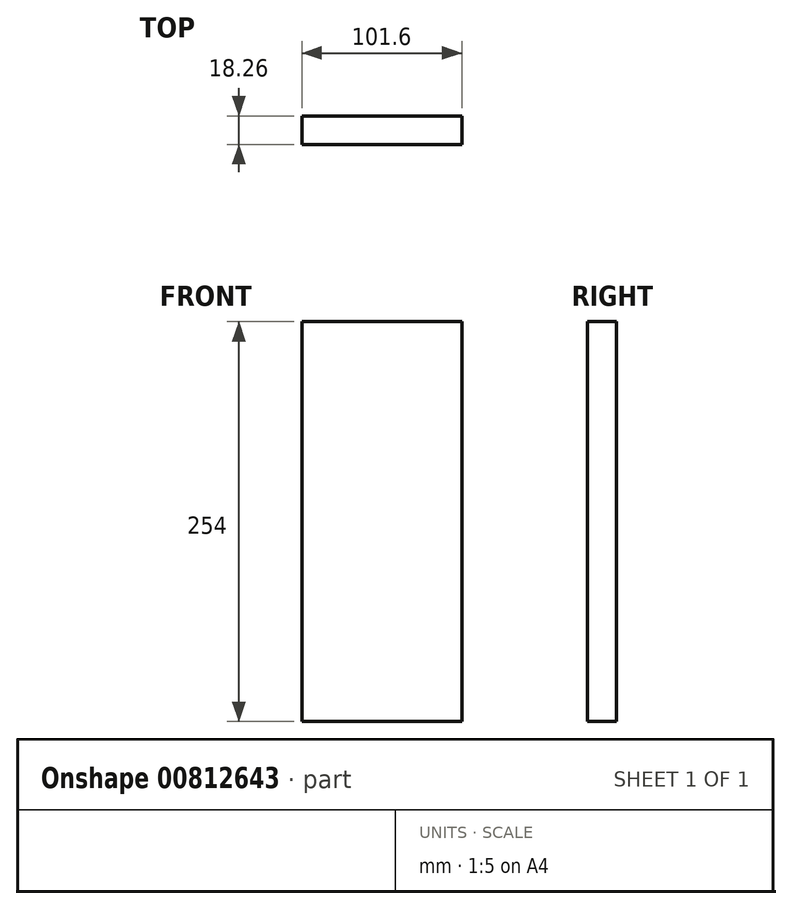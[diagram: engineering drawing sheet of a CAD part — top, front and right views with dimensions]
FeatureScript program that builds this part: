
annotation { "Feature Type Name" : "Feature", "Feature Type Description" : "" }
export const myFeature = defineFeature(function(context is Context, id is Id, definition is map)
    precondition{}
    {
        {
            var Q0;
            Q0=qCreatedBy(makeId("Front.planeOp"),FACE);
            var sketch = newSketch(context, id + "F0", { "sketchPlane" : qUnion([Q0])});
            skLineSegment(sketch, "E0.bottom", {"start": v(50.8, 127) * mm, "end": v(-50.8, 127) * mm});
            skLineSegment(sketch, "E0.top", {"start": v(50.8, -127) * mm, "end": v(-50.8, -127) * mm});
            skLineSegment(sketch, "E0.left", {"start": v(50.8, 127) * mm, "end": v(50.8, -127) * mm});
            skLineSegment(sketch, "E0.right", {"start": v(-50.8, 127) * mm, "end": v(-50.8, -127) * mm});
            skPoint(sketch, "E0.middle", {"position": v(0, 0) * mm});
            skSolve(sketch);
        }
        {
            var Q0;
            Q0=qSketchRegion(id+"F0",true);
            extrude(context, id + "F1", {"entities" : qUnion([Q0]), "depth" : 18.26 * mm, "offsetDistance" : 25.4 * mm});
        }
    });
